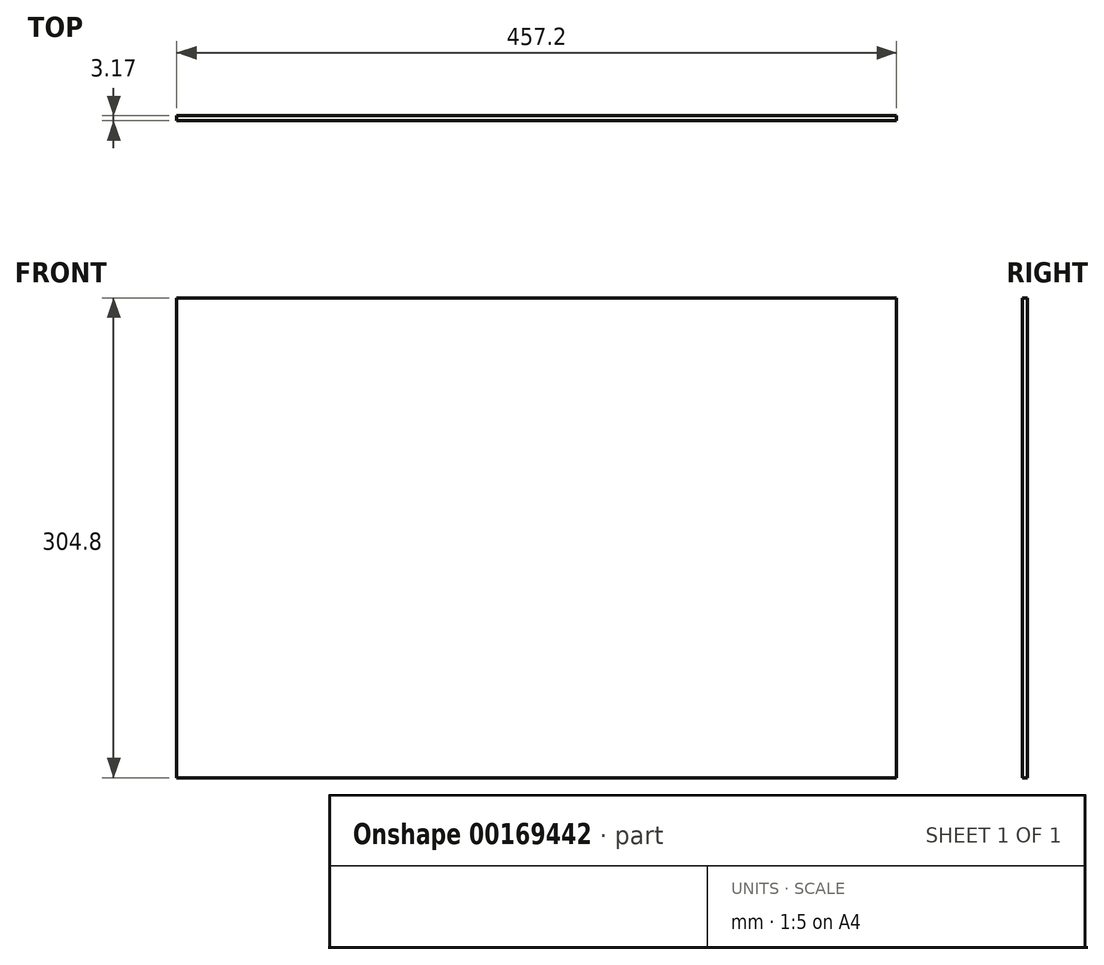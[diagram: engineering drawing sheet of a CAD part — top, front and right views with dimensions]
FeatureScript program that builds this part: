
annotation { "Feature Type Name" : "Feature", "Feature Type Description" : "" }
export const myFeature = defineFeature(function(context is Context, id is Id, definition is map)
    precondition{}
    {
        {
            var Q0;
            Q0=qCreatedBy(makeId("Front.planeOp"),FACE);
            var sketch = newSketch(context, id + "F0", { "sketchPlane" : qUnion([Q0])});
            skLineSegment(sketch, "E0.bottom", {"start": v(228.6, 152.4) * mm, "end": v(-228.6, 152.4) * mm});
            skLineSegment(sketch, "E0.top", {"start": v(228.6, -152.4) * mm, "end": v(-228.6, -152.4) * mm});
            skLineSegment(sketch, "E0.left", {"start": v(228.6, 152.4) * mm, "end": v(228.6, -152.4) * mm});
            skLineSegment(sketch, "E0.right", {"start": v(-228.6, 152.4) * mm, "end": v(-228.6, -152.4) * mm});
            skPoint(sketch, "E0.middle", {"position": v(0, 0) * mm});
            skSolve(sketch);
        }
        {
            var Q0;
            Q0 = qSketchRegion(id + "F0", true);
            extrude(context, id + "F1", {"entities" : qUnion([Q0]), "depth" : 3.17 * mm});
        }
    });
